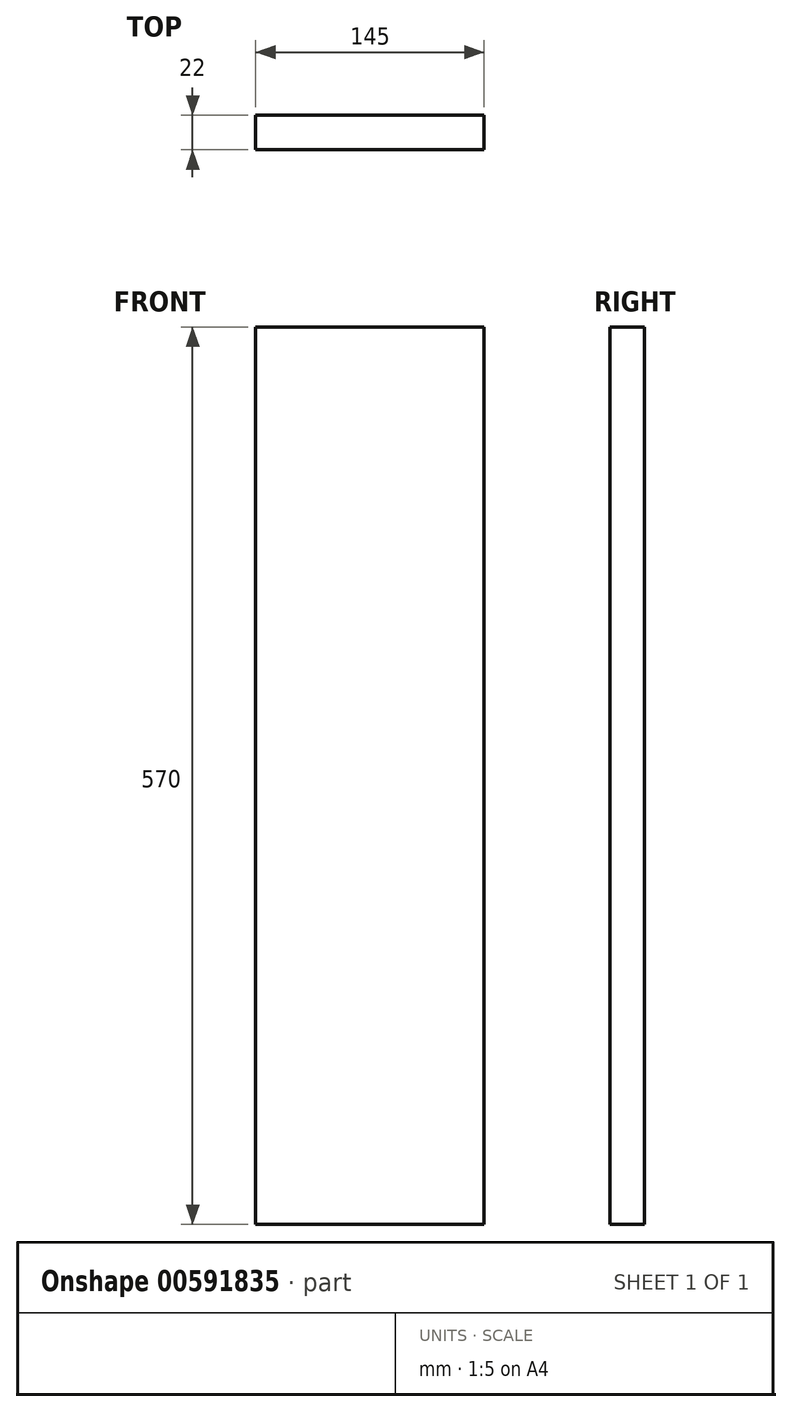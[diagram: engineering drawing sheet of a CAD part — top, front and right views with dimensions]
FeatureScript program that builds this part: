
annotation { "Feature Type Name" : "Feature", "Feature Type Description" : "" }
export const myFeature = defineFeature(function(context is Context, id is Id, definition is map)
    precondition{}
    {
        {
            var Q0;
            Q0=qCreatedBy(makeId("Top.planeOp"),FACE);
            var sketch = newSketch(context, id + "F0", { "sketchPlane" : qUnion([Q0])});
            skLineSegment(sketch, "E0.bottom", {"start": v(0, 0) * mm, "end": v(145, 0) * mm});
            skLineSegment(sketch, "E0.top", {"start": v(0, 22) * mm, "end": v(145, 22) * mm});
            skLineSegment(sketch, "E0.left", {"start": v(0, 0) * mm, "end": v(0, 22) * mm});
            skLineSegment(sketch, "E0.right", {"start": v(145, 0) * mm, "end": v(145, 22) * mm});
            skSolve(sketch);
        }
        {
            var Q0;
            Q0=makeQuery(id+"F0.imprint","IMPRINT",FACE,{"disambiguationData":[TD([[makeQuery(id+"F0.imprint","IMPRINT",EDGE,{"derivedFrom":sQuery(id+"F0.wireOp",EDGE,"E0.bottom")}),1.0]])]});
            extrude(context, id + "F1", {"entities" : qUnion([Q0]), "depth" : 570 * mm, "offsetDistance" : 25 * mm});
        }
    });
